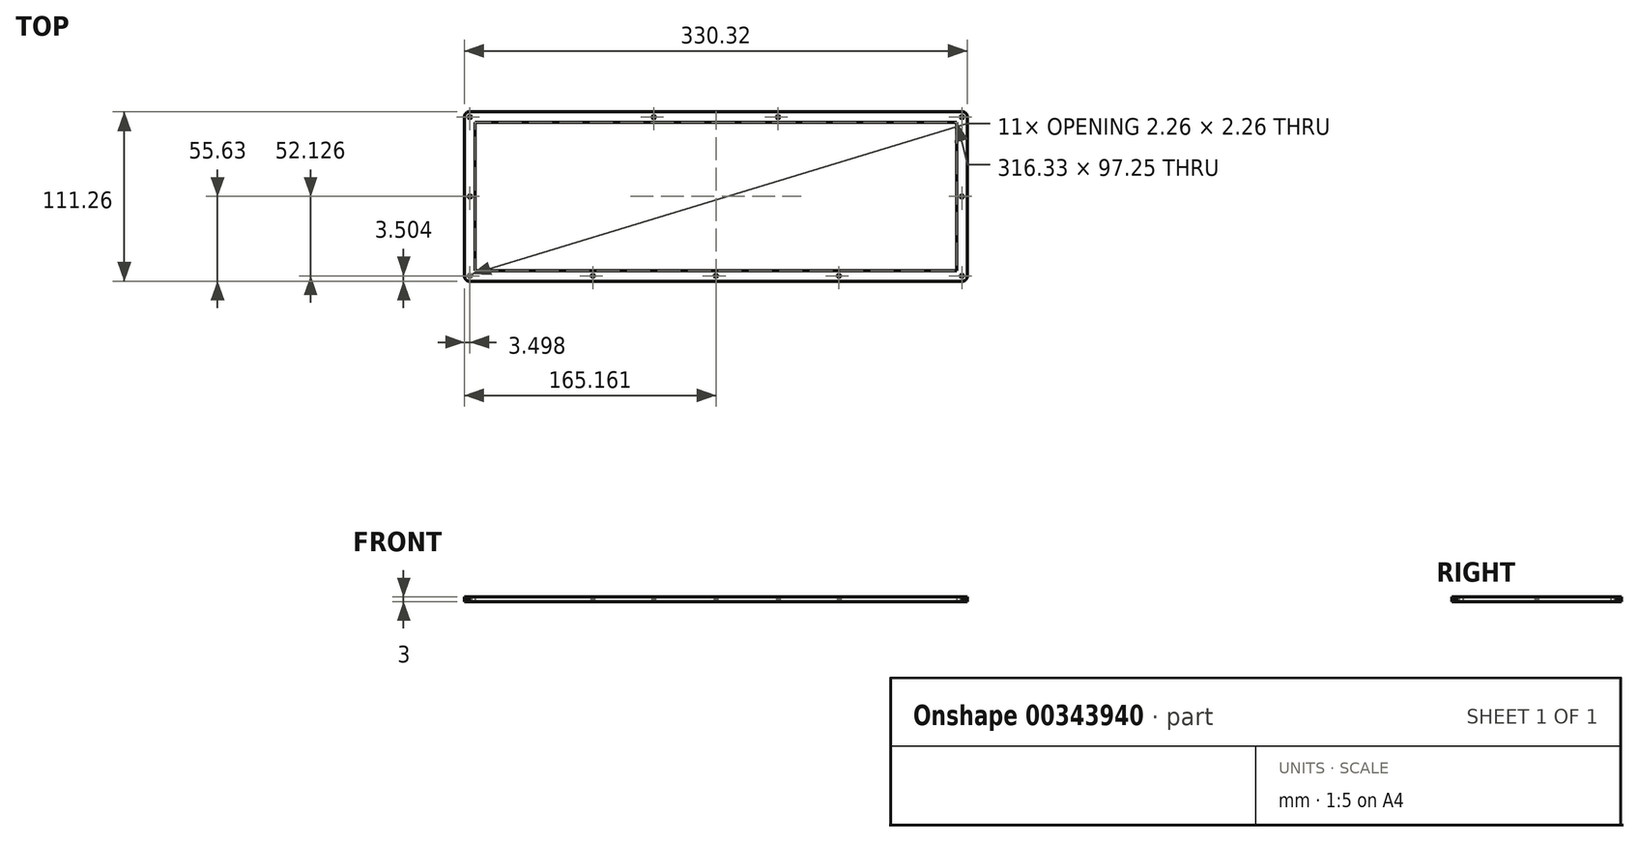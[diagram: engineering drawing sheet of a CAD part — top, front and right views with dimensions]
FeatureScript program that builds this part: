
annotation { "Feature Type Name" : "Feature", "Feature Type Description" : "" }
export const myFeature = defineFeature(function(context is Context, id is Id, definition is map)
    precondition{}
    {
        {
            var Q0;
            Q0=qCreatedBy(makeId("Top.planeOp"),FACE);
            var sketch = newSketch(context, id + "F0", { "sketchPlane" : qUnion([Q0])});
            skLineSegment(sketch, "E0", {"start": v(162.16, 55.62) * mm, "end": v(162.4, 55.62) * mm});
            skLineSegment(sketch, "E1", {"start": v(162.4, 55.62) * mm, "end": v(162.63, 55.59) * mm});
            skLineSegment(sketch, "E2", {"start": v(162.63, 55.59) * mm, "end": v(162.86, 55.54) * mm});
            skLineSegment(sketch, "E3", {"start": v(162.86, 55.54) * mm, "end": v(163.1, 55.48) * mm});
            skLineSegment(sketch, "E4", {"start": v(163.1, 55.48) * mm, "end": v(163.31, 55.4) * mm});
            skLineSegment(sketch, "E5", {"start": v(163.31, 55.4) * mm, "end": v(163.53, 55.3) * mm});
            skLineSegment(sketch, "E6", {"start": v(163.53, 55.3) * mm, "end": v(163.73, 55.18) * mm});
            skLineSegment(sketch, "E7", {"start": v(163.73, 55.18) * mm, "end": v(163.93, 55.05) * mm});
            skLineSegment(sketch, "E8", {"start": v(163.93, 55.05) * mm, "end": v(164.11, 54.9) * mm});
            skLineSegment(sketch, "E9", {"start": v(164.11, 54.9) * mm, "end": v(164.29, 54.75) * mm});
            skLineSegment(sketch, "E10", {"start": v(164.29, 54.75) * mm, "end": v(164.45, 54.57) * mm});
            skLineSegment(sketch, "E11", {"start": v(164.45, 54.57) * mm, "end": v(164.6, 54.39) * mm});
            skLineSegment(sketch, "E12", {"start": v(164.6, 54.39) * mm, "end": v(164.72, 54.2) * mm});
            skLineSegment(sketch, "E13", {"start": v(164.72, 54.2) * mm, "end": v(164.84, 53.99) * mm});
            skLineSegment(sketch, "E14", {"start": v(164.84, 53.99) * mm, "end": v(164.93, 53.77) * mm});
            skLineSegment(sketch, "E15", {"start": v(164.93, 53.77) * mm, "end": v(165.02, 53.55) * mm});
            skLineSegment(sketch, "E16", {"start": v(165.02, 53.55) * mm, "end": v(165.08, 53.33) * mm});
            skLineSegment(sketch, "E17", {"start": v(165.08, 53.33) * mm, "end": v(165.13, 53.1) * mm});
            skLineSegment(sketch, "E18", {"start": v(165.13, 53.1) * mm, "end": v(165.15, 52.86) * mm});
            skLineSegment(sketch, "E19", {"start": v(165.15, 52.86) * mm, "end": v(165.16, 52.62) * mm});
            skLineSegment(sketch, "E20", {"start": v(165.16, 52.62) * mm, "end": v(165.16, -52.63) * mm});
            skLineSegment(sketch, "E21", {"start": v(165.16, -52.63) * mm, "end": v(165.15, -52.86) * mm});
            skLineSegment(sketch, "E22", {"start": v(165.15, -52.86) * mm, "end": v(165.13, -53.1) * mm});
            skLineSegment(sketch, "E23", {"start": v(165.13, -53.1) * mm, "end": v(165.08, -53.33) * mm});
            skLineSegment(sketch, "E24", {"start": v(165.08, -53.33) * mm, "end": v(165.02, -53.55) * mm});
            skLineSegment(sketch, "E25", {"start": v(165.02, -53.55) * mm, "end": v(164.93, -53.77) * mm});
            skLineSegment(sketch, "E26", {"start": v(164.93, -53.77) * mm, "end": v(164.84, -53.99) * mm});
            skLineSegment(sketch, "E27", {"start": v(164.84, -53.99) * mm, "end": v(164.72, -54.2) * mm});
            skLineSegment(sketch, "E28", {"start": v(164.72, -54.2) * mm, "end": v(164.6, -54.39) * mm});
            skLineSegment(sketch, "E29", {"start": v(164.6, -54.39) * mm, "end": v(164.45, -54.57) * mm});
            skLineSegment(sketch, "E30", {"start": v(164.45, -54.57) * mm, "end": v(164.29, -54.75) * mm});
            skLineSegment(sketch, "E31", {"start": v(164.29, -54.75) * mm, "end": v(164.11, -54.9) * mm});
            skLineSegment(sketch, "E32", {"start": v(164.11, -54.9) * mm, "end": v(163.93, -55.05) * mm});
            skLineSegment(sketch, "E33", {"start": v(163.93, -55.05) * mm, "end": v(163.73, -55.18) * mm});
            skLineSegment(sketch, "E34", {"start": v(163.73, -55.18) * mm, "end": v(163.53, -55.3) * mm});
            skLineSegment(sketch, "E35", {"start": v(163.53, -55.3) * mm, "end": v(163.31, -55.4) * mm});
            skLineSegment(sketch, "E36", {"start": v(163.31, -55.4) * mm, "end": v(163.1, -55.48) * mm});
            skLineSegment(sketch, "E37", {"start": v(163.1, -55.48) * mm, "end": v(162.86, -55.54) * mm});
            skLineSegment(sketch, "E38", {"start": v(162.86, -55.54) * mm, "end": v(162.63, -55.59) * mm});
            skLineSegment(sketch, "E39", {"start": v(162.63, -55.59) * mm, "end": v(162.4, -55.62) * mm});
            skLineSegment(sketch, "E40", {"start": v(162.4, -55.62) * mm, "end": v(162.16, -55.63) * mm});
            skLineSegment(sketch, "E41", {"start": v(162.16, -55.63) * mm, "end": v(-162.16, -55.63) * mm});
            skLineSegment(sketch, "E42", {"start": v(-162.16, -55.63) * mm, "end": v(-162.4, -55.62) * mm});
            skLineSegment(sketch, "E43", {"start": v(-162.4, -55.62) * mm, "end": v(-162.63, -55.59) * mm});
            skLineSegment(sketch, "E44", {"start": v(-162.63, -55.59) * mm, "end": v(-162.86, -55.54) * mm});
            skLineSegment(sketch, "E45", {"start": v(-162.86, -55.54) * mm, "end": v(-163.09, -55.48) * mm});
            skLineSegment(sketch, "E46", {"start": v(-163.09, -55.48) * mm, "end": v(-163.31, -55.4) * mm});
            skLineSegment(sketch, "E47", {"start": v(-163.31, -55.4) * mm, "end": v(-163.52, -55.3) * mm});
            skLineSegment(sketch, "E48", {"start": v(-163.52, -55.3) * mm, "end": v(-163.73, -55.18) * mm});
            skLineSegment(sketch, "E49", {"start": v(-163.73, -55.18) * mm, "end": v(-163.93, -55.05) * mm});
            skLineSegment(sketch, "E50", {"start": v(-163.93, -55.05) * mm, "end": v(-164.11, -54.9) * mm});
            skLineSegment(sketch, "E51", {"start": v(-164.11, -54.9) * mm, "end": v(-164.28, -54.75) * mm});
            skLineSegment(sketch, "E52", {"start": v(-164.28, -54.75) * mm, "end": v(-164.44, -54.57) * mm});
            skLineSegment(sketch, "E53", {"start": v(-164.44, -54.57) * mm, "end": v(-164.6, -54.39) * mm});
            skLineSegment(sketch, "E54", {"start": v(-164.6, -54.39) * mm, "end": v(-164.72, -54.2) * mm});
            skLineSegment(sketch, "E55", {"start": v(-164.72, -54.2) * mm, "end": v(-164.84, -53.99) * mm});
            skLineSegment(sketch, "E56", {"start": v(-164.84, -53.99) * mm, "end": v(-164.93, -53.77) * mm});
            skLineSegment(sketch, "E57", {"start": v(-164.93, -53.77) * mm, "end": v(-165.02, -53.55) * mm});
            skLineSegment(sketch, "E58", {"start": v(-165.02, -53.55) * mm, "end": v(-165.08, -53.33) * mm});
            skLineSegment(sketch, "E59", {"start": v(-165.08, -53.33) * mm, "end": v(-165.13, -53.1) * mm});
            skLineSegment(sketch, "E60", {"start": v(-165.13, -53.1) * mm, "end": v(-165.15, -52.86) * mm});
            skLineSegment(sketch, "E61", {"start": v(-165.15, -52.86) * mm, "end": v(-165.16, -52.63) * mm});
            skLineSegment(sketch, "E62", {"start": v(-165.16, -52.63) * mm, "end": v(-165.16, 52.62) * mm});
            skLineSegment(sketch, "E63", {"start": v(-165.16, 52.62) * mm, "end": v(-165.15, 52.86) * mm});
            skLineSegment(sketch, "E64", {"start": v(-165.15, 52.86) * mm, "end": v(-165.13, 53.1) * mm});
            skLineSegment(sketch, "E65", {"start": v(-165.13, 53.1) * mm, "end": v(-165.08, 53.33) * mm});
            skLineSegment(sketch, "E66", {"start": v(-165.08, 53.33) * mm, "end": v(-165.02, 53.55) * mm});
            skLineSegment(sketch, "E67", {"start": v(-165.02, 53.55) * mm, "end": v(-164.93, 53.77) * mm});
            skLineSegment(sketch, "E68", {"start": v(-164.93, 53.77) * mm, "end": v(-164.84, 53.99) * mm});
            skLineSegment(sketch, "E69", {"start": v(-164.84, 53.99) * mm, "end": v(-164.72, 54.2) * mm});
            skLineSegment(sketch, "E70", {"start": v(-164.72, 54.2) * mm, "end": v(-164.6, 54.39) * mm});
            skLineSegment(sketch, "E71", {"start": v(-164.6, 54.39) * mm, "end": v(-164.44, 54.57) * mm});
            skLineSegment(sketch, "E72", {"start": v(-164.44, 54.57) * mm, "end": v(-164.28, 54.75) * mm});
            skLineSegment(sketch, "E73", {"start": v(-164.28, 54.75) * mm, "end": v(-164.11, 54.9) * mm});
            skLineSegment(sketch, "E74", {"start": v(-164.11, 54.9) * mm, "end": v(-163.93, 55.05) * mm});
            skLineSegment(sketch, "E75", {"start": v(-163.93, 55.05) * mm, "end": v(-163.73, 55.18) * mm});
            skLineSegment(sketch, "E76", {"start": v(-163.73, 55.18) * mm, "end": v(-163.52, 55.3) * mm});
            skLineSegment(sketch, "E77", {"start": v(-163.52, 55.3) * mm, "end": v(-163.31, 55.4) * mm});
            skLineSegment(sketch, "E78", {"start": v(-163.31, 55.4) * mm, "end": v(-163.09, 55.48) * mm});
            skLineSegment(sketch, "E79", {"start": v(-163.09, 55.48) * mm, "end": v(-162.86, 55.54) * mm});
            skLineSegment(sketch, "E80", {"start": v(-162.86, 55.54) * mm, "end": v(-162.63, 55.59) * mm});
            skLineSegment(sketch, "E81", {"start": v(-162.63, 55.59) * mm, "end": v(-162.4, 55.62) * mm});
            skLineSegment(sketch, "E82", {"start": v(-162.4, 55.62) * mm, "end": v(-162.16, 55.63) * mm});
            skLineSegment(sketch, "E83", {"start": v(-162.16, 55.63) * mm, "end": v(162.16, 55.62) * mm});
            skLineSegment(sketch, "E84", {"start": v(161.31, -51.05) * mm, "end": v(161, -51.21) * mm});
            skLineSegment(sketch, "E85", {"start": v(161, -51.21) * mm, "end": v(160.75, -51.46) * mm});
            skLineSegment(sketch, "E86", {"start": v(160.75, -51.46) * mm, "end": v(160.59, -51.78) * mm});
            skLineSegment(sketch, "E87", {"start": v(160.59, -51.78) * mm, "end": v(160.53, -52.13) * mm});
            skLineSegment(sketch, "E88", {"start": v(160.53, -52.13) * mm, "end": v(160.59, -52.48) * mm});
            skLineSegment(sketch, "E89", {"start": v(160.59, -52.48) * mm, "end": v(160.75, -52.79) * mm});
            skLineSegment(sketch, "E90", {"start": v(160.75, -52.79) * mm, "end": v(161, -53.04) * mm});
            skLineSegment(sketch, "E91", {"start": v(161, -53.04) * mm, "end": v(161.31, -53.2) * mm});
            skLineSegment(sketch, "E92", {"start": v(161.31, -53.2) * mm, "end": v(161.66, -53.26) * mm});
            skLineSegment(sketch, "E93", {"start": v(161.66, -53.26) * mm, "end": v(162.01, -53.2) * mm});
            skLineSegment(sketch, "E94", {"start": v(162.01, -53.2) * mm, "end": v(162.33, -53.04) * mm});
            skLineSegment(sketch, "E95", {"start": v(162.33, -53.04) * mm, "end": v(162.58, -52.79) * mm});
            skLineSegment(sketch, "E96", {"start": v(162.58, -52.79) * mm, "end": v(162.74, -52.48) * mm});
            skLineSegment(sketch, "E97", {"start": v(162.74, -52.48) * mm, "end": v(162.8, -52.13) * mm});
            skLineSegment(sketch, "E98", {"start": v(162.8, -52.13) * mm, "end": v(162.74, -51.78) * mm});
            skLineSegment(sketch, "E99", {"start": v(162.74, -51.78) * mm, "end": v(162.58, -51.46) * mm});
            skLineSegment(sketch, "E100", {"start": v(162.58, -51.46) * mm, "end": v(162.33, -51.21) * mm});
            skLineSegment(sketch, "E101", {"start": v(162.33, -51.21) * mm, "end": v(162.01, -51.05) * mm});
            skLineSegment(sketch, "E102", {"start": v(162.01, -51.05) * mm, "end": v(161.66, -51) * mm});
            skLineSegment(sketch, "E103", {"start": v(161.66, -51) * mm, "end": v(161.31, -51.05) * mm});
            skLineSegment(sketch, "E104", {"start": v(80.48, -51.05) * mm, "end": v(80.17, -51.21) * mm});
            skLineSegment(sketch, "E105", {"start": v(80.17, -51.21) * mm, "end": v(79.92, -51.46) * mm});
            skLineSegment(sketch, "E106", {"start": v(79.92, -51.46) * mm, "end": v(79.76, -51.78) * mm});
            skLineSegment(sketch, "E107", {"start": v(79.76, -51.78) * mm, "end": v(79.7, -52.13) * mm});
            skLineSegment(sketch, "E108", {"start": v(79.7, -52.13) * mm, "end": v(79.76, -52.48) * mm});
            skLineSegment(sketch, "E109", {"start": v(79.76, -52.48) * mm, "end": v(79.92, -52.79) * mm});
            skLineSegment(sketch, "E110", {"start": v(79.92, -52.79) * mm, "end": v(80.17, -53.04) * mm});
            skLineSegment(sketch, "E111", {"start": v(80.17, -53.04) * mm, "end": v(80.48, -53.2) * mm});
            skLineSegment(sketch, "E112", {"start": v(80.48, -53.2) * mm, "end": v(80.83, -53.26) * mm});
            skLineSegment(sketch, "E113", {"start": v(80.83, -53.26) * mm, "end": v(81.18, -53.2) * mm});
            skLineSegment(sketch, "E114", {"start": v(81.18, -53.2) * mm, "end": v(81.5, -53.04) * mm});
            skLineSegment(sketch, "E115", {"start": v(81.5, -53.04) * mm, "end": v(81.75, -52.79) * mm});
            skLineSegment(sketch, "E116", {"start": v(81.75, -52.79) * mm, "end": v(81.9, -52.48) * mm});
            skLineSegment(sketch, "E117", {"start": v(81.9, -52.48) * mm, "end": v(81.96, -52.13) * mm});
            skLineSegment(sketch, "E118", {"start": v(81.96, -52.13) * mm, "end": v(81.9, -51.78) * mm});
            skLineSegment(sketch, "E119", {"start": v(81.9, -51.78) * mm, "end": v(81.75, -51.46) * mm});
            skLineSegment(sketch, "E120", {"start": v(81.75, -51.46) * mm, "end": v(81.5, -51.21) * mm});
            skLineSegment(sketch, "E121", {"start": v(81.5, -51.21) * mm, "end": v(81.18, -51.05) * mm});
            skLineSegment(sketch, "E122", {"start": v(81.18, -51.05) * mm, "end": v(80.83, -51) * mm});
            skLineSegment(sketch, "E123", {"start": v(80.83, -51) * mm, "end": v(80.48, -51.05) * mm});
            skLineSegment(sketch, "E124", {"start": v(-0.35, -51.05) * mm, "end": v(-0.66, -51.21) * mm});
            skLineSegment(sketch, "E125", {"start": v(-0.66, -51.21) * mm, "end": v(-0.91, -51.46) * mm});
            skLineSegment(sketch, "E126", {"start": v(-0.91, -51.46) * mm, "end": v(-1.07, -51.78) * mm});
            skLineSegment(sketch, "E127", {"start": v(-1.07, -51.78) * mm, "end": v(-1.13, -52.13) * mm});
            skLineSegment(sketch, "E128", {"start": v(-1.13, -52.13) * mm, "end": v(-1.07, -52.48) * mm});
            skLineSegment(sketch, "E129", {"start": v(-1.07, -52.48) * mm, "end": v(-0.91, -52.79) * mm});
            skLineSegment(sketch, "E130", {"start": v(-0.91, -52.79) * mm, "end": v(-0.66, -53.04) * mm});
            skLineSegment(sketch, "E131", {"start": v(-0.66, -53.04) * mm, "end": v(-0.35, -53.2) * mm});
            skLineSegment(sketch, "E132", {"start": v(-0.35, -53.2) * mm, "end": v(0, -53.26) * mm});
            skLineSegment(sketch, "E133", {"start": v(0, -53.26) * mm, "end": v(0.35, -53.2) * mm});
            skLineSegment(sketch, "E134", {"start": v(0.35, -53.2) * mm, "end": v(0.67, -53.04) * mm});
            skLineSegment(sketch, "E135", {"start": v(0.67, -53.04) * mm, "end": v(0.92, -52.79) * mm});
            skLineSegment(sketch, "E136", {"start": v(0.92, -52.79) * mm, "end": v(1.07, -52.48) * mm});
            skLineSegment(sketch, "E137", {"start": v(1.07, -52.48) * mm, "end": v(1.13, -52.13) * mm});
            skLineSegment(sketch, "E138", {"start": v(1.13, -52.13) * mm, "end": v(1.07, -51.78) * mm});
            skLineSegment(sketch, "E139", {"start": v(1.07, -51.78) * mm, "end": v(0.92, -51.46) * mm});
            skLineSegment(sketch, "E140", {"start": v(0.92, -51.46) * mm, "end": v(0.67, -51.21) * mm});
            skLineSegment(sketch, "E141", {"start": v(0.67, -51.21) * mm, "end": v(0.35, -51.05) * mm});
            skLineSegment(sketch, "E142", {"start": v(0.35, -51.05) * mm, "end": v(0, -51) * mm});
            skLineSegment(sketch, "E143", {"start": v(0, -51) * mm, "end": v(-0.35, -51.05) * mm});
            skLineSegment(sketch, "E144", {"start": v(-81.18, -51.05) * mm, "end": v(-81.5, -51.21) * mm});
            skLineSegment(sketch, "E145", {"start": v(-81.5, -51.21) * mm, "end": v(-81.75, -51.46) * mm});
            skLineSegment(sketch, "E146", {"start": v(-81.75, -51.46) * mm, "end": v(-81.9, -51.78) * mm});
            skLineSegment(sketch, "E147", {"start": v(-81.9, -51.78) * mm, "end": v(-81.96, -52.13) * mm});
            skLineSegment(sketch, "E148", {"start": v(-81.96, -52.13) * mm, "end": v(-81.9, -52.48) * mm});
            skLineSegment(sketch, "E149", {"start": v(-81.9, -52.48) * mm, "end": v(-81.75, -52.79) * mm});
            skLineSegment(sketch, "E150", {"start": v(-81.75, -52.79) * mm, "end": v(-81.5, -53.04) * mm});
            skLineSegment(sketch, "E151", {"start": v(-81.5, -53.04) * mm, "end": v(-81.18, -53.2) * mm});
            skLineSegment(sketch, "E152", {"start": v(-81.18, -53.2) * mm, "end": v(-80.83, -53.26) * mm});
            skLineSegment(sketch, "E153", {"start": v(-80.83, -53.26) * mm, "end": v(-80.48, -53.2) * mm});
            skLineSegment(sketch, "E154", {"start": v(-80.48, -53.2) * mm, "end": v(-80.17, -53.04) * mm});
            skLineSegment(sketch, "E155", {"start": v(-80.17, -53.04) * mm, "end": v(-79.92, -52.79) * mm});
            skLineSegment(sketch, "E156", {"start": v(-79.92, -52.79) * mm, "end": v(-79.76, -52.48) * mm});
            skLineSegment(sketch, "E157", {"start": v(-79.76, -52.48) * mm, "end": v(-79.7, -52.13) * mm});
            skLineSegment(sketch, "E158", {"start": v(-79.7, -52.13) * mm, "end": v(-79.76, -51.78) * mm});
            skLineSegment(sketch, "E159", {"start": v(-79.76, -51.78) * mm, "end": v(-79.92, -51.46) * mm});
            skLineSegment(sketch, "E160", {"start": v(-79.92, -51.46) * mm, "end": v(-80.17, -51.21) * mm});
            skLineSegment(sketch, "E161", {"start": v(-80.17, -51.21) * mm, "end": v(-80.48, -51.05) * mm});
            skLineSegment(sketch, "E162", {"start": v(-80.48, -51.05) * mm, "end": v(-80.83, -51) * mm});
            skLineSegment(sketch, "E163", {"start": v(-80.83, -51) * mm, "end": v(-81.18, -51.05) * mm});
            skLineSegment(sketch, "E164", {"start": v(-162.01, -51.05) * mm, "end": v(-162.33, -51.21) * mm});
            skLineSegment(sketch, "E165", {"start": v(-162.33, -51.21) * mm, "end": v(-162.58, -51.46) * mm});
            skLineSegment(sketch, "E166", {"start": v(-162.58, -51.46) * mm, "end": v(-162.74, -51.78) * mm});
            skLineSegment(sketch, "E167", {"start": v(-162.74, -51.78) * mm, "end": v(-162.8, -52.13) * mm});
            skLineSegment(sketch, "E168", {"start": v(-162.8, -52.13) * mm, "end": v(-162.74, -52.48) * mm});
            skLineSegment(sketch, "E169", {"start": v(-162.74, -52.48) * mm, "end": v(-162.58, -52.79) * mm});
            skLineSegment(sketch, "E170", {"start": v(-162.58, -52.79) * mm, "end": v(-162.33, -53.04) * mm});
            skLineSegment(sketch, "E171", {"start": v(-162.33, -53.04) * mm, "end": v(-162.01, -53.2) * mm});
            skLineSegment(sketch, "E172", {"start": v(-162.01, -53.2) * mm, "end": v(-161.66, -53.26) * mm});
            skLineSegment(sketch, "E173", {"start": v(-161.66, -53.26) * mm, "end": v(-161.31, -53.2) * mm});
            skLineSegment(sketch, "E174", {"start": v(-161.31, -53.2) * mm, "end": v(-161, -53.04) * mm});
            skLineSegment(sketch, "E175", {"start": v(-161, -53.04) * mm, "end": v(-160.75, -52.79) * mm});
            skLineSegment(sketch, "E176", {"start": v(-160.75, -52.79) * mm, "end": v(-160.59, -52.48) * mm});
            skLineSegment(sketch, "E177", {"start": v(-160.59, -52.48) * mm, "end": v(-160.53, -52.13) * mm});
            skLineSegment(sketch, "E178", {"start": v(-160.53, -52.13) * mm, "end": v(-160.59, -51.78) * mm});
            skLineSegment(sketch, "E179", {"start": v(-160.59, -51.78) * mm, "end": v(-160.75, -51.46) * mm});
            skLineSegment(sketch, "E180", {"start": v(-160.75, -51.46) * mm, "end": v(-161, -51.21) * mm});
            skLineSegment(sketch, "E181", {"start": v(-161, -51.21) * mm, "end": v(-161.31, -51.05) * mm});
            skLineSegment(sketch, "E182", {"start": v(-161.31, -51.05) * mm, "end": v(-161.66, -51) * mm});
            skLineSegment(sketch, "E183", {"start": v(-161.66, -51) * mm, "end": v(-162.01, -51.05) * mm});
            skLineSegment(sketch, "E184", {"start": v(-158.16, 48.62) * mm, "end": v(158.16, 48.62) * mm});
            skLineSegment(sketch, "E185", {"start": v(158.16, 48.62) * mm, "end": v(158.16, -48.63) * mm});
            skLineSegment(sketch, "E186", {"start": v(158.16, -48.63) * mm, "end": v(-158.16, -48.63) * mm});
            skLineSegment(sketch, "E187", {"start": v(-158.16, -48.63) * mm, "end": v(-158.16, 48.62) * mm});
            skLineSegment(sketch, "E188", {"start": v(161.31, 1.08) * mm, "end": v(161, 0.91) * mm});
            skLineSegment(sketch, "E189", {"start": v(161, 0.91) * mm, "end": v(160.75, 0.66) * mm});
            skLineSegment(sketch, "E190", {"start": v(160.75, 0.66) * mm, "end": v(160.59, 0.35) * mm});
            skLineSegment(sketch, "E191", {"start": v(160.59, 0.35) * mm, "end": v(160.53, 0) * mm});
            skLineSegment(sketch, "E192", {"start": v(160.53, 0) * mm, "end": v(160.59, -0.35) * mm});
            skLineSegment(sketch, "E193", {"start": v(160.59, -0.35) * mm, "end": v(160.75, -0.66) * mm});
            skLineSegment(sketch, "E194", {"start": v(160.75, -0.66) * mm, "end": v(161, -0.91) * mm});
            skLineSegment(sketch, "E195", {"start": v(161, -0.91) * mm, "end": v(161.31, -1.07) * mm});
            skLineSegment(sketch, "E196", {"start": v(161.31, -1.07) * mm, "end": v(161.66, -1.13) * mm});
            skLineSegment(sketch, "E197", {"start": v(161.66, -1.13) * mm, "end": v(162.01, -1.07) * mm});
            skLineSegment(sketch, "E198", {"start": v(162.01, -1.07) * mm, "end": v(162.33, -0.91) * mm});
            skLineSegment(sketch, "E199", {"start": v(162.33, -0.91) * mm, "end": v(162.58, -0.66) * mm});
            skLineSegment(sketch, "E200", {"start": v(162.58, -0.66) * mm, "end": v(162.74, -0.35) * mm});
            skLineSegment(sketch, "E201", {"start": v(162.74, -0.35) * mm, "end": v(162.8, 0) * mm});
            skLineSegment(sketch, "E202", {"start": v(162.8, 0) * mm, "end": v(162.74, 0.35) * mm});
            skLineSegment(sketch, "E203", {"start": v(162.74, 0.35) * mm, "end": v(162.58, 0.66) * mm});
            skLineSegment(sketch, "E204", {"start": v(162.58, 0.66) * mm, "end": v(162.33, 0.91) * mm});
            skLineSegment(sketch, "E205", {"start": v(162.33, 0.91) * mm, "end": v(162.01, 1.08) * mm});
            skLineSegment(sketch, "E206", {"start": v(162.01, 1.08) * mm, "end": v(161.66, 1.13) * mm});
            skLineSegment(sketch, "E207", {"start": v(161.66, 1.13) * mm, "end": v(161.31, 1.08) * mm});
            skLineSegment(sketch, "E208", {"start": v(-162.01, 1.08) * mm, "end": v(-162.33, 0.91) * mm});
            skLineSegment(sketch, "E209", {"start": v(-162.33, 0.91) * mm, "end": v(-162.58, 0.66) * mm});
            skLineSegment(sketch, "E210", {"start": v(-162.58, 0.66) * mm, "end": v(-162.74, 0.35) * mm});
            skLineSegment(sketch, "E211", {"start": v(-162.74, 0.35) * mm, "end": v(-162.8, 0) * mm});
            skLineSegment(sketch, "E212", {"start": v(-162.8, 0) * mm, "end": v(-162.74, -0.35) * mm});
            skLineSegment(sketch, "E213", {"start": v(-162.74, -0.35) * mm, "end": v(-162.58, -0.66) * mm});
            skLineSegment(sketch, "E214", {"start": v(-162.58, -0.66) * mm, "end": v(-162.33, -0.91) * mm});
            skLineSegment(sketch, "E215", {"start": v(-162.33, -0.91) * mm, "end": v(-162.01, -1.07) * mm});
            skLineSegment(sketch, "E216", {"start": v(-162.01, -1.07) * mm, "end": v(-161.66, -1.13) * mm});
            skLineSegment(sketch, "E217", {"start": v(-161.66, -1.13) * mm, "end": v(-161.31, -1.07) * mm});
            skLineSegment(sketch, "E218", {"start": v(-161.31, -1.07) * mm, "end": v(-161, -0.91) * mm});
            skLineSegment(sketch, "E219", {"start": v(-161, -0.91) * mm, "end": v(-160.75, -0.66) * mm});
            skLineSegment(sketch, "E220", {"start": v(-160.75, -0.66) * mm, "end": v(-160.59, -0.35) * mm});
            skLineSegment(sketch, "E221", {"start": v(-160.59, -0.35) * mm, "end": v(-160.53, 0) * mm});
            skLineSegment(sketch, "E222", {"start": v(-160.53, 0) * mm, "end": v(-160.59, 0.35) * mm});
            skLineSegment(sketch, "E223", {"start": v(-160.59, 0.35) * mm, "end": v(-160.75, 0.66) * mm});
            skLineSegment(sketch, "E224", {"start": v(-160.75, 0.66) * mm, "end": v(-161, 0.91) * mm});
            skLineSegment(sketch, "E225", {"start": v(-161, 0.91) * mm, "end": v(-161.31, 1.08) * mm});
            skLineSegment(sketch, "E226", {"start": v(-161.31, 1.08) * mm, "end": v(-161.66, 1.13) * mm});
            skLineSegment(sketch, "E227", {"start": v(-161.66, 1.13) * mm, "end": v(-162.01, 1.08) * mm});
            skLineSegment(sketch, "E228", {"start": v(-41.18, 53.2) * mm, "end": v(-41.5, 53.04) * mm});
            skLineSegment(sketch, "E229", {"start": v(-41.5, 53.04) * mm, "end": v(-41.75, 52.8) * mm});
            skLineSegment(sketch, "E230", {"start": v(-41.75, 52.8) * mm, "end": v(-41.9, 52.47) * mm});
            skLineSegment(sketch, "E231", {"start": v(-41.9, 52.47) * mm, "end": v(-41.96, 52.12) * mm});
            skLineSegment(sketch, "E232", {"start": v(-41.96, 52.12) * mm, "end": v(-41.9, 51.78) * mm});
            skLineSegment(sketch, "E233", {"start": v(-41.9, 51.78) * mm, "end": v(-41.75, 51.46) * mm});
            skLineSegment(sketch, "E234", {"start": v(-41.75, 51.46) * mm, "end": v(-41.5, 51.21) * mm});
            skLineSegment(sketch, "E235", {"start": v(-41.5, 51.21) * mm, "end": v(-41.18, 51.05) * mm});
            skLineSegment(sketch, "E236", {"start": v(-41.18, 51.05) * mm, "end": v(-40.83, 51) * mm});
            skLineSegment(sketch, "E237", {"start": v(-40.83, 51) * mm, "end": v(-40.48, 51.05) * mm});
            skLineSegment(sketch, "E238", {"start": v(-40.48, 51.05) * mm, "end": v(-40.17, 51.21) * mm});
            skLineSegment(sketch, "E239", {"start": v(-40.17, 51.21) * mm, "end": v(-39.92, 51.46) * mm});
            skLineSegment(sketch, "E240", {"start": v(-39.92, 51.46) * mm, "end": v(-39.76, 51.78) * mm});
            skLineSegment(sketch, "E241", {"start": v(-39.76, 51.78) * mm, "end": v(-39.7, 52.12) * mm});
            skLineSegment(sketch, "E242", {"start": v(-39.7, 52.12) * mm, "end": v(-39.76, 52.47) * mm});
            skLineSegment(sketch, "E243", {"start": v(-39.76, 52.47) * mm, "end": v(-39.92, 52.8) * mm});
            skLineSegment(sketch, "E244", {"start": v(-39.92, 52.8) * mm, "end": v(-40.17, 53.04) * mm});
            skLineSegment(sketch, "E245", {"start": v(-40.17, 53.04) * mm, "end": v(-40.48, 53.2) * mm});
            skLineSegment(sketch, "E246", {"start": v(-40.48, 53.2) * mm, "end": v(-40.83, 53.26) * mm});
            skLineSegment(sketch, "E247", {"start": v(-40.83, 53.26) * mm, "end": v(-41.18, 53.2) * mm});
            skLineSegment(sketch, "E248", {"start": v(40.48, 53.2) * mm, "end": v(40.17, 53.04) * mm});
            skLineSegment(sketch, "E249", {"start": v(40.17, 53.04) * mm, "end": v(39.92, 52.8) * mm});
            skLineSegment(sketch, "E250", {"start": v(39.92, 52.8) * mm, "end": v(39.76, 52.47) * mm});
            skLineSegment(sketch, "E251", {"start": v(39.76, 52.47) * mm, "end": v(39.7, 52.12) * mm});
            skLineSegment(sketch, "E252", {"start": v(39.7, 52.12) * mm, "end": v(39.76, 51.78) * mm});
            skLineSegment(sketch, "E253", {"start": v(39.76, 51.78) * mm, "end": v(39.92, 51.46) * mm});
            skLineSegment(sketch, "E254", {"start": v(39.92, 51.46) * mm, "end": v(40.17, 51.21) * mm});
            skLineSegment(sketch, "E255", {"start": v(40.17, 51.21) * mm, "end": v(40.48, 51.05) * mm});
            skLineSegment(sketch, "E256", {"start": v(40.48, 51.05) * mm, "end": v(40.83, 51) * mm});
            skLineSegment(sketch, "E257", {"start": v(40.83, 51) * mm, "end": v(41.18, 51.05) * mm});
            skLineSegment(sketch, "E258", {"start": v(41.18, 51.05) * mm, "end": v(41.5, 51.21) * mm});
            skLineSegment(sketch, "E259", {"start": v(41.5, 51.21) * mm, "end": v(41.75, 51.46) * mm});
            skLineSegment(sketch, "E260", {"start": v(41.75, 51.46) * mm, "end": v(41.9, 51.78) * mm});
            skLineSegment(sketch, "E261", {"start": v(41.9, 51.78) * mm, "end": v(41.96, 52.12) * mm});
            skLineSegment(sketch, "E262", {"start": v(41.96, 52.12) * mm, "end": v(41.9, 52.47) * mm});
            skLineSegment(sketch, "E263", {"start": v(41.9, 52.47) * mm, "end": v(41.75, 52.8) * mm});
            skLineSegment(sketch, "E264", {"start": v(41.75, 52.8) * mm, "end": v(41.5, 53.04) * mm});
            skLineSegment(sketch, "E265", {"start": v(41.5, 53.04) * mm, "end": v(41.18, 53.2) * mm});
            skLineSegment(sketch, "E266", {"start": v(41.18, 53.2) * mm, "end": v(40.83, 53.26) * mm});
            skLineSegment(sketch, "E267", {"start": v(40.83, 53.26) * mm, "end": v(40.48, 53.2) * mm});
            skLineSegment(sketch, "E268", {"start": v(161.31, 53.2) * mm, "end": v(161, 53.04) * mm});
            skLineSegment(sketch, "E269", {"start": v(161, 53.04) * mm, "end": v(160.75, 52.8) * mm});
            skLineSegment(sketch, "E270", {"start": v(160.75, 52.8) * mm, "end": v(160.59, 52.47) * mm});
            skLineSegment(sketch, "E271", {"start": v(160.59, 52.47) * mm, "end": v(160.53, 52.12) * mm});
            skLineSegment(sketch, "E272", {"start": v(160.53, 52.12) * mm, "end": v(160.59, 51.78) * mm});
            skLineSegment(sketch, "E273", {"start": v(160.59, 51.78) * mm, "end": v(160.75, 51.46) * mm});
            skLineSegment(sketch, "E274", {"start": v(160.75, 51.46) * mm, "end": v(161, 51.21) * mm});
            skLineSegment(sketch, "E275", {"start": v(161, 51.21) * mm, "end": v(161.31, 51.05) * mm});
            skLineSegment(sketch, "E276", {"start": v(161.31, 51.05) * mm, "end": v(161.66, 51) * mm});
            skLineSegment(sketch, "E277", {"start": v(161.66, 51) * mm, "end": v(162.01, 51.05) * mm});
            skLineSegment(sketch, "E278", {"start": v(162.01, 51.05) * mm, "end": v(162.33, 51.21) * mm});
            skLineSegment(sketch, "E279", {"start": v(162.33, 51.21) * mm, "end": v(162.58, 51.46) * mm});
            skLineSegment(sketch, "E280", {"start": v(162.58, 51.46) * mm, "end": v(162.74, 51.78) * mm});
            skLineSegment(sketch, "E281", {"start": v(162.74, 51.78) * mm, "end": v(162.8, 52.12) * mm});
            skLineSegment(sketch, "E282", {"start": v(162.8, 52.12) * mm, "end": v(162.74, 52.47) * mm});
            skLineSegment(sketch, "E283", {"start": v(162.74, 52.47) * mm, "end": v(162.58, 52.8) * mm});
            skLineSegment(sketch, "E284", {"start": v(162.58, 52.8) * mm, "end": v(162.33, 53.04) * mm});
            skLineSegment(sketch, "E285", {"start": v(162.33, 53.04) * mm, "end": v(162.01, 53.2) * mm});
            skLineSegment(sketch, "E286", {"start": v(162.01, 53.2) * mm, "end": v(161.66, 53.26) * mm});
            skLineSegment(sketch, "E287", {"start": v(161.66, 53.26) * mm, "end": v(161.31, 53.2) * mm});
            skLineSegment(sketch, "E288", {"start": v(-162.01, 53.2) * mm, "end": v(-162.33, 53.04) * mm});
            skLineSegment(sketch, "E289", {"start": v(-162.33, 53.04) * mm, "end": v(-162.58, 52.8) * mm});
            skLineSegment(sketch, "E290", {"start": v(-162.58, 52.8) * mm, "end": v(-162.74, 52.47) * mm});
            skLineSegment(sketch, "E291", {"start": v(-162.74, 52.47) * mm, "end": v(-162.8, 52.12) * mm});
            skLineSegment(sketch, "E292", {"start": v(-162.8, 52.12) * mm, "end": v(-162.74, 51.78) * mm});
            skLineSegment(sketch, "E293", {"start": v(-162.74, 51.78) * mm, "end": v(-162.58, 51.46) * mm});
            skLineSegment(sketch, "E294", {"start": v(-162.58, 51.46) * mm, "end": v(-162.33, 51.21) * mm});
            skLineSegment(sketch, "E295", {"start": v(-162.33, 51.21) * mm, "end": v(-162.01, 51.05) * mm});
            skLineSegment(sketch, "E296", {"start": v(-162.01, 51.05) * mm, "end": v(-161.66, 51) * mm});
            skLineSegment(sketch, "E297", {"start": v(-161.66, 51) * mm, "end": v(-161.31, 51.05) * mm});
            skLineSegment(sketch, "E298", {"start": v(-161.31, 51.05) * mm, "end": v(-161, 51.21) * mm});
            skLineSegment(sketch, "E299", {"start": v(-161, 51.21) * mm, "end": v(-160.75, 51.46) * mm});
            skLineSegment(sketch, "E300", {"start": v(-160.75, 51.46) * mm, "end": v(-160.59, 51.78) * mm});
            skLineSegment(sketch, "E301", {"start": v(-160.59, 51.78) * mm, "end": v(-160.53, 52.12) * mm});
            skLineSegment(sketch, "E302", {"start": v(-160.53, 52.12) * mm, "end": v(-160.59, 52.47) * mm});
            skLineSegment(sketch, "E303", {"start": v(-160.59, 52.47) * mm, "end": v(-160.75, 52.8) * mm});
            skLineSegment(sketch, "E304", {"start": v(-160.75, 52.8) * mm, "end": v(-161, 53.04) * mm});
            skLineSegment(sketch, "E305", {"start": v(-161, 53.04) * mm, "end": v(-161.31, 53.2) * mm});
            skLineSegment(sketch, "E306", {"start": v(-161.31, 53.2) * mm, "end": v(-161.66, 53.26) * mm});
            skLineSegment(sketch, "E307", {"start": v(-161.66, 53.26) * mm, "end": v(-162.01, 53.2) * mm});
            skSolve(sketch);
        }
        {
            var Q0;
            Q0 = qSketchRegion(id + "F0", true);
            extrude(context, id + "F1", {"entities" : qUnion([Q0]), "depth" : 3 * mm});
        }
    });
